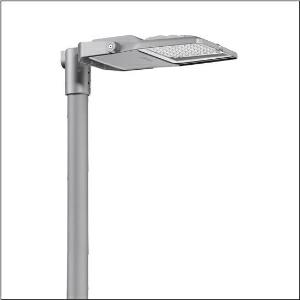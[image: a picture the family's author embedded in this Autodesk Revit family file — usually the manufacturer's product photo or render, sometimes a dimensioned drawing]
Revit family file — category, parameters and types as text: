
# Revit family: floodlight_fl_21_iq_mini___pl52_5xa7772d4d3a_25ab
name_source: partatom
category: Lighting Fixtures
units: mm (PartAtom-declared; Revit-internal decimal feet)

## family parameters
Cut with Voids When Loaded = No
Host = Face
Light Source = No
Part Type = Normal
Room Calculation Point = No
Round Connector Dimension = Use Diameter
Shared = No

## types (1)
- --- (1 x LED, 18610 lm, 143 W, 4000K)
    Apparent Load = 143 VA
    CIE Flux Codes = 26 60 98 100 100
    Color Rendering = 70
    Color Temperature = 4000K
    Default Elevation = 1800 mm
    Description = Floodlight FL 21 iQ mini, floodlight, primary light control with lens, of PMMA, primary optical cover: protective disc, of toughened safety glass, transparent, light distribution: PL52, light emission: direct distribution, installation type: surface-mounted, lamps: LED, High Power LED, rated values: 18.610lm | 143W | 130,1lm/W (begin service life); end service life: 18.610lm | 151,6W; at 50% lumin. flux: 9.305lm | 60,8W | 153lm/W, colour temperature: 4000K, colour rendering: CRI > 70, light colour: 740, light setting 1 begin service life: 100% | 18.610lm | 143W | 130,1lm/W | 4.000K, light setting 1 end service life: 151,6W, further light settings possible, control: pre-setting: linear dimming characteristic, Auto-Match, Temp-Guard, Night-Set, Smart-Wire, Desk-Remote (wireless, voltage-free reading and setting of iQ features in the workshop via application-optimized NFC function/RFID function), optimised constant luminous flux control (CLO 2.0), Light-Fading, Lumen-Switch, with terminal, 6-pole, mains connection: 220..240V, AC, 50/60Hz, luminaire housing, of diecast aluminium, powder-coated, SITECO metallic grey (DB 702S), corrosivity category C5 mid according to DIN EN ISO 12944suitable for swimming poolschlorine-resistant, sealing non-destructively replaceable, please order mast flange separately, mast bracket, of steel, galvanised, powder-coated, protection rating (complete): IP66, insulation class (complete): insulation class II (safety insulation), certification: CE, ENEC, VDE, protection symbol: D, impact resistance: IK08, permissible operating ambient temperature: -40..+40°C, permissible operating ambient temperature for outdoor applications: -40..+50°C, standard: DIN EN 12944, LABS conformity tested according to VDMA 24364:2018-05, packaging unit: 1 piece

Light Distribution: PL52
    Height = 70 mm
    Lamp = 1 x LED
    Lamp Light Flux = 18610 lm
    Lamp Power = 143 W
    Lamp count = 1
    Length = 485 mm
    Luminous efficacy = 130 lm/W
    Manufacturer = Siteco
    ModVariant = No
    Model = 5XA7772D4D3A
    Mounting Place = Pole
    Mounting Type = Pole annexe
    Number of Poles = 1
    OnlyDefault = Yes
    Power Factor = 1
    Product Name = Floodlight FL 21 iQ mini | PL52
    Product group = floodlight | pylon annexe
    ProductGroupID = 6201
    Protection Class = Protection class II
    Protection Degree = IP 66
    RLX_Detail_Level = 1
    RLX_Emergency_Light_Flux = 0 lm
    RLX_Emergency_Type = 0
    RLX_Emergency_Type_DB = No
    RlxData = <blob elided: 102045 chars, md5=a67c9ef8>
    Socket = socket
    Standby Power = 0 W
    System Light Flux = 18610 lm
    System Power = 143 W
    Type Comments = factory setting: luminous flux: 100 % | dim-lin: 254 | 730 mA
    Type Image = l_1007125.jpg
    URL = http://relux.com
    VarID = @adj_164585
    Voltage = 0 V
    Weight = 0.00 kg
    Width = 337 mm

## geometry (parser evidence)
native form markers: Blend x4, Sweep x11
no freeform markers — native parametric forms only
